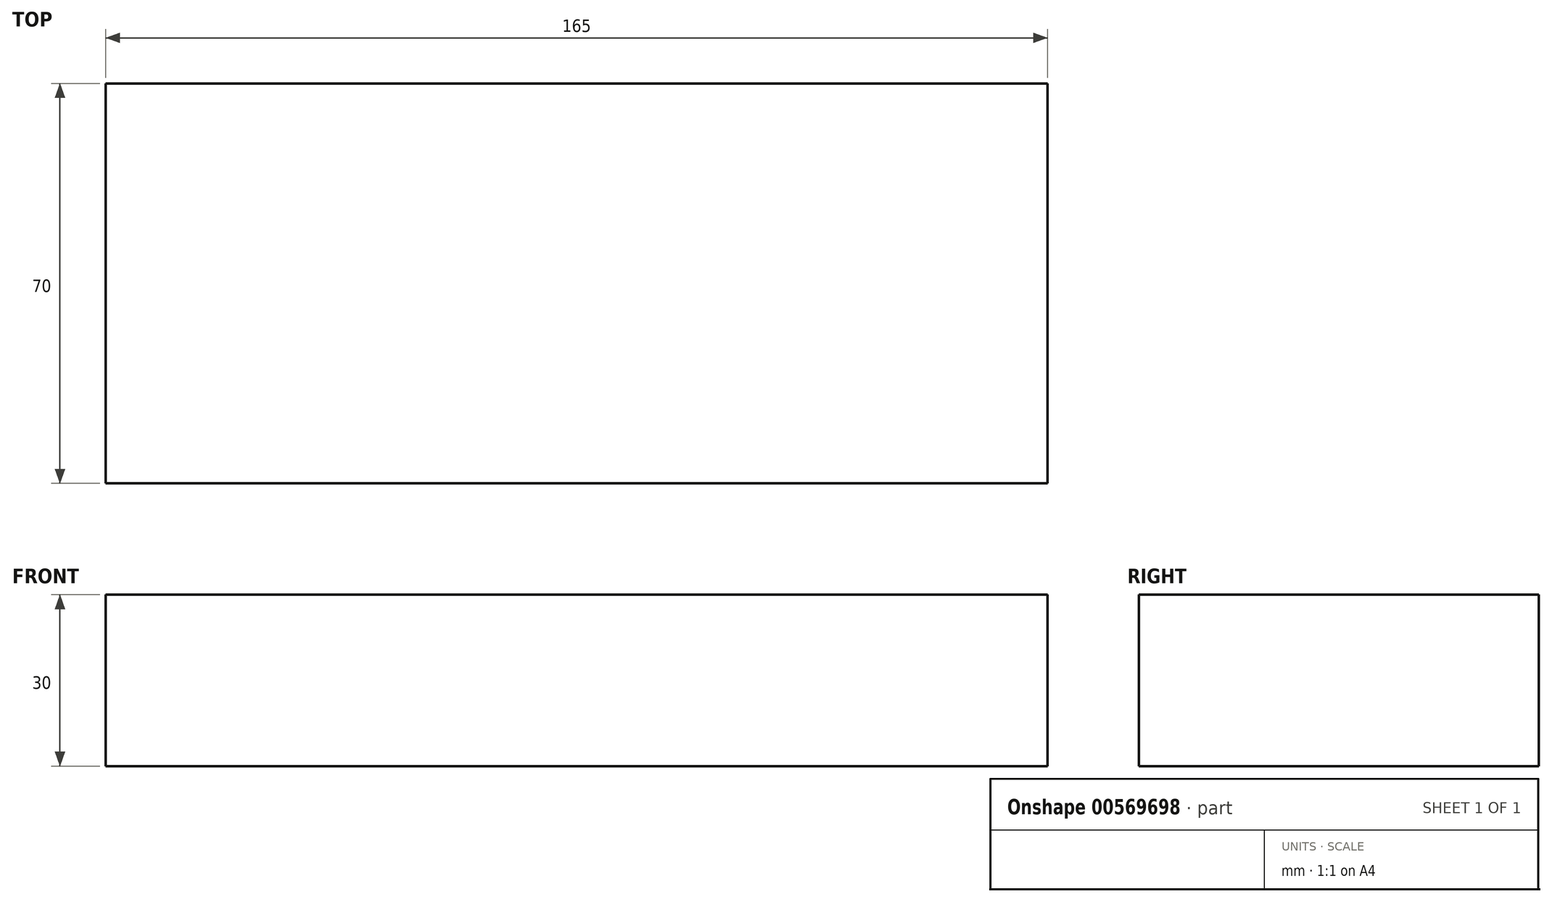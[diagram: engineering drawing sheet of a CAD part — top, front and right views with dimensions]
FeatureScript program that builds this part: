
annotation { "Feature Type Name" : "Feature", "Feature Type Description" : "" }
export const myFeature = defineFeature(function(context is Context, id is Id, definition is map)
    precondition{}
    {
        {
            var Q0;
            Q0=qCreatedBy(makeId("Top.planeOp"),FACE);
            var sketch = newSketch(context, id + "F0", { "sketchPlane" : qUnion([Q0])});
            skLineSegment(sketch, "E0.bottom", {"start": v(-82.5, 35) * mm, "end": v(82.5, 35) * mm});
            skLineSegment(sketch, "E0.top", {"start": v(-82.5, -35) * mm, "end": v(82.5, -35) * mm});
            skLineSegment(sketch, "E0.left", {"start": v(-82.5, 35) * mm, "end": v(-82.5, -35) * mm});
            skLineSegment(sketch, "E0.right", {"start": v(82.5, 35) * mm, "end": v(82.5, -35) * mm});
            skSolve(sketch);
        }
        {
            var Q0;
            Q0 = qSketchRegion(id + "F0", true);
            extrude(context, id + "F1", {"entities" : qUnion([Q0]), "depth" : 30 * mm, "offsetDistance" : 25 * mm});
        }
    });
